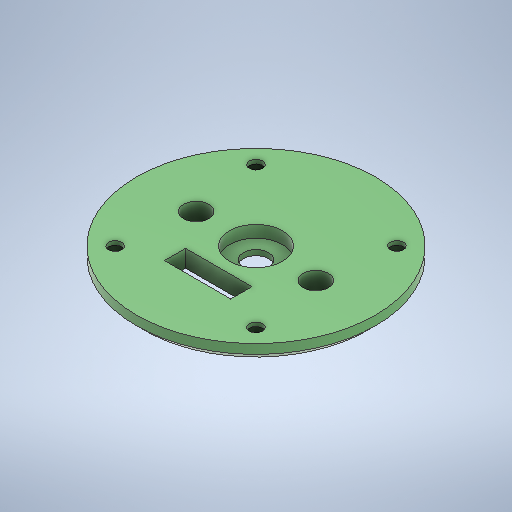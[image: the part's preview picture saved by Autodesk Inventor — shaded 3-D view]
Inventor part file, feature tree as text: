
AUTODESK INVENTOR PART (.ipt)
format: ipt  version: 2025.2 (Build 292293000, 293)  size: 297,984 bytes
history: native  units: mm
features: sketch x2, extrude x2, hole x1, chamfer x1
ambient origin geometry x8: Origin, YZ Plane, XZ Plane, XY Plane, X Axis, Y Axis, Z Axis, Center Point
bodies: Solid1 (feature_tree)
feature tree (6):
  sketch  "Sketch1"  dims[d0=90.0mm d1=20.0mm]
  extrude  "Extrusion1"  Depth=20.0mm
  extrude  "Extrusion2"  Depth=2.0mm TaperAngle=0.0deg
  hole  "Hole1"  [1 undecoded]
  chamfer  "Chamfer1"  Distance=37.5mm
  sketch  "Sketch2"  dims[d2=45.0mm d4=2.0mm d5=0.0mm d6=4.5mm d7=0.0mm d9=37.5mm d10=45.0deg d11=5.0mm d12=6.0mm d13=7.2mm d14=5.0mm d15=90.0deg d16=8.0mm d17=20.594885mm d20=18.0mm d21=8.0mm d22=25.0mm d23=3.0mm d24=2.0mm d25=45.0deg d26=9.5mm]
note: 1 required parameter value undecoded (feature->parameter linkage not recoverable at this tier; creation-order binding heuristic only, values carry confidence <= 0.55)
